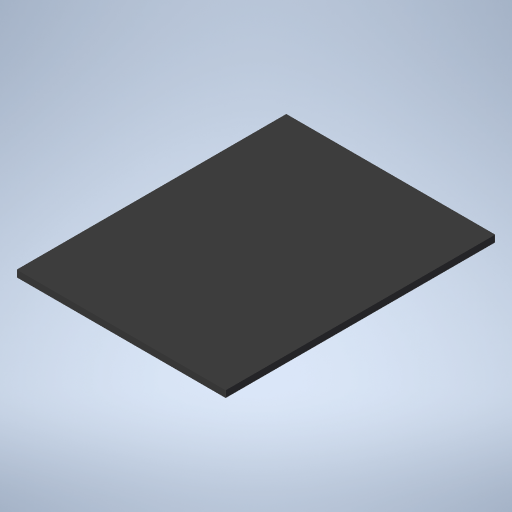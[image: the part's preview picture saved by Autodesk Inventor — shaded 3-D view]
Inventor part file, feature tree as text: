
AUTODESK INVENTOR PART (.ipt)
format: ipt  version: 2024.3 (Build 283343000, 343)  size: 208,384 bytes
history: native  units: mm
features: extrude x1, sketch x1
ambient origin geometry x8: Origin, YZ Plane, XZ Plane, XY Plane, X Axis, Y Axis, Z Axis, Center Point
bodies: Solid1 (feature_tree)
feature tree (2):
  extrude  "Extrusion1"  Depth=93.0mm
  sketch  "Sketch1"  dims[d0=120.0mm d1=93.0mm d2=3.0mm d3=0.0mm]
